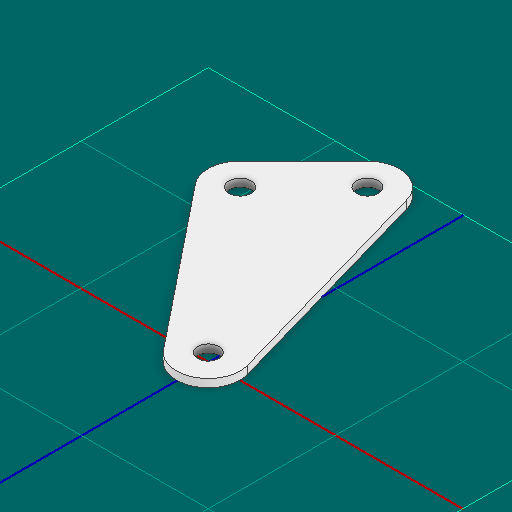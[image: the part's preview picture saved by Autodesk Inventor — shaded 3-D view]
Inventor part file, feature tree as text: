
AUTODESK INVENTOR PART (.ipt)
format: ipt  version: 2025 (Build 290162000, 162)  size: 106,496 bytes
history: native  units: in
note: dims shown in document units (in); Inventor stores cm internally (conversion verified against a paired STEP export)
features: other x3, extrude x1, sketch x1
ambient origin geometry x8: Origin, YZ Plane, XZ Plane, XY Plane, X Axis, Y Axis, Z Axis, Center Point
bodies: Solid1 (feature_tree)
feature tree (5):
  other  "Blocks"
  extrude  "Extrusion1"  Depth=0.0625in TaperAngle=0.0deg
  sketch  "Sketch1"  dims[d0=0.5in d1=0.5in d2=0.0625in d3=0.0in]
  other  "main"
  other  "main:1"
